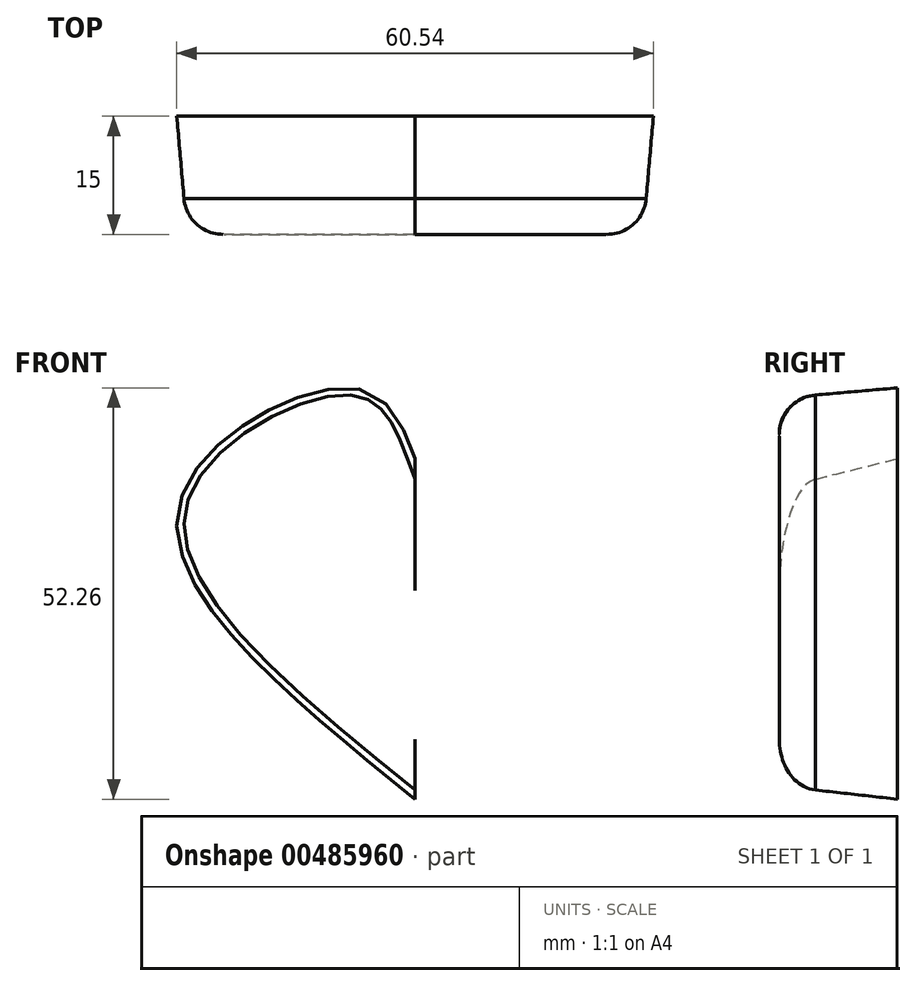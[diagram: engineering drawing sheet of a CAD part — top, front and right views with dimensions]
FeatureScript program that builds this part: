
annotation { "Feature Type Name" : "Feature", "Feature Type Description" : "" }
export const myFeature = defineFeature(function(context is Context, id is Id, definition is map)
    precondition{}
    {
        {
            var Q0;
            Q0=qCreatedBy(makeId("Front.planeOp"),FACE);
            var sketch = newSketch(context, id + "F0", { "sketchPlane" : qUnion([Q0])});
            skFitSpline(sketch, "E0", {"points": [v(0, 2.52) * mm, v(-29.87, 40.34) * mm, v(-7.56, 54.7) * mm, v(0, 45.78) * mm], "startDerivative": vector(-110.85, 89.46) * mm, "endDerivative": vector(21.22, -56.44) * mm});
            skFitSpline(sketch, "E1.MirrorCS", {"points": [v(0, 2.52) * mm, v(29.87, 40.34) * mm, v(7.56, 54.7) * mm, v(0, 45.78) * mm], "startDerivative": vector(110.85, 89.46) * mm, "endDerivative": vector(-21.22, -56.44) * mm});
            skSolve(sketch);
        }
        {
            var Q0;
            Q0=makeQuery(id+"F0.imprint","IMPRINT",FACE,{"disambiguationData":[TD([[makeQuery(id+"F0.imprint","IMPRINT",EDGE,{"derivedFrom":sQuery(id+"F0.wireOp",EDGE,"E0")}),-1.0]])]});
            extrude(context, id + "F1", {"entities" : qUnion([Q0]), "depth" : 15 * mm, "hasDraft" : true, "draftAngle" : 5 * degree, "draftPullDirection" : true});
        }
        {
            var Q0;
            Q0=makeQuery(id+"F1.opExtrude","CAP_EDGE",EDGE,{"disambiguationData":[OSD([sQuery(id+"F0.wireOp",EDGE,"E0")])],"isStart":false});
            var Q1;
            Q1=makeQuery(id+"F1.opExtrude","CAP_EDGE",EDGE,{"disambiguationData":[OSD([sQuery(id+"F0.wireOp",EDGE,"E1.MirrorCS")])],"isStart":false});
            fillet(context, id + "F2", {"entities" : qUnion([Q0, Q1]), "radius" : 5 * mm, "tangentPropagation" : true, "allowEdgeOverflow" : false});
        }
    });
